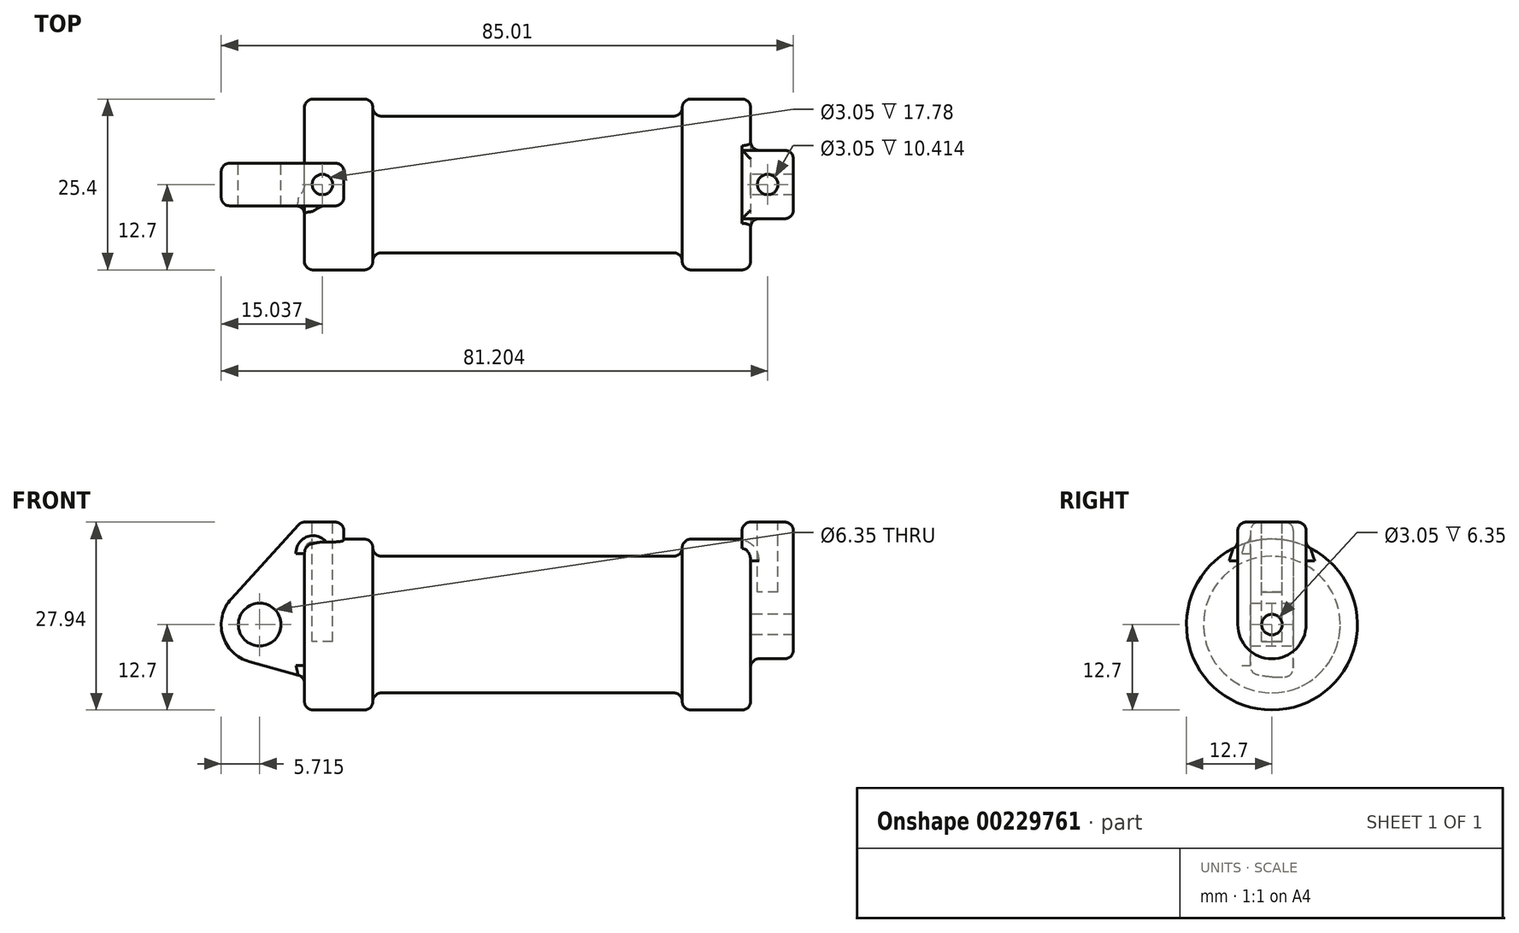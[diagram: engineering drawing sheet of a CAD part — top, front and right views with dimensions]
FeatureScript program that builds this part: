
annotation { "Feature Type Name" : "Feature", "Feature Type Description" : "" }
export const myFeature = defineFeature(function(context is Context, id is Id, definition is map)
    precondition{}
    {
        {
            var Q0;
            Q0=qCreatedBy(makeId("Front.planeOp"),FACE);
            var sketch = newSketch(context, id + "F0", { "sketchPlane" : qUnion([Q0])});
            skLineSegment(sketch, "E0", {"start": v(0, 0) * mm, "end": v(0, 12.7) * mm});
            skLineSegment(sketch, "E1", {"start": v(0, 12.7) * mm, "end": v(10.16, 12.7) * mm});
            skLineSegment(sketch, "E2", {"start": v(10.16, 12.7) * mm, "end": v(10.16, 10.16) * mm});
            skLineSegment(sketch, "E3", {"start": v(10.16, 10.16) * mm, "end": v(56.13, 10.16) * mm});
            skLineSegment(sketch, "E4", {"start": v(56.13, 10.16) * mm, "end": v(56.13, 12.7) * mm});
            skLineSegment(sketch, "E5", {"start": v(56.13, 12.7) * mm, "end": v(66.3, 12.7) * mm});
            skLineSegment(sketch, "E6", {"start": v(66.3, 12.7) * mm, "end": v(66.3, 0) * mm});
            skLineSegment(sketch, "E7", {"start": v(66.3, 0) * mm, "end": v(0, 0) * mm});
            skLineSegment(sketch, "E8", {"start": v(5.84, 15.24) * mm, "end": v(-0.5, 15.24) * mm});
            skLineSegment(sketch, "E9", {"start": v(-0.5, 15.24) * mm, "end": v(-10.88, 3.85) * mm});
            skLineSegment(sketch, "E10", {"start": v(0, 0) * mm, "end": v(-6.65, 0) * mm});
            skCircle(sketch, "E11", {"center": v(-6.65, 0) * mm, "radius": 5.72 * mm});
            skCircle(sketch, "E12", {"center": v(-6.65, 0) * mm, "radius": 3.18 * mm});
            skLineSegment(sketch, "E13", {"start": v(5.84, 15.24) * mm, "end": v(5.84, -9.4) * mm});
            skLineSegment(sketch, "E14", {"start": v(5.84, -9.4) * mm, "end": v(-8.18, -5.5) * mm});
            skSolve(sketch);
        }
        {
            var Q0;
            {var subQ0=sQuery(id+"F0.wireOp",EDGE,"E0");Q0=makeQuery(id+"F0.imprint","IMPRINT",FACE,{"disambiguationData":[TD([[makeQuery(id+"F0.imprint","IMPRINT",EDGE,{"derivedFrom":subQ0}),-1.0]])]});}
            var Q1;
            {var subQ0=sQuery(id+"F0.wireOp",EDGE,"E2");Q1=makeQuery(id+"F0.imprint","IMPRINT",FACE,{"disambiguationData":[TD([[makeQuery(id+"F0.imprint","IMPRINT",EDGE,{"derivedFrom":subQ0}),-1.0]])]});}
            var Q2;
            Q2=sQuery(id+"F0.wireOp",EDGE,"E7");
            revolve(context, id + "F1", {"entities" : qUnion([Q0, Q1]), "axis" : qUnion([Q2]), "revolveType" : RevolveType.FULL});
        }
        {
            var Q0;
            {var subQ3=sQuery(id+"F0.wireOp",EDGE,"E0");Q0=makeQuery(id+"F0.imprint","IMPRINT",FACE,{"disambiguationData":[TD([[makeQuery(id+"F0.imprint","IMPRINT",EDGE,{"derivedFrom":subQ3}),1.0]])]});}
            var Q1;
            {var subQ0=sQuery(id+"F0.wireOp",EDGE,"E0");Q1=makeQuery(id+"F0.imprint","IMPRINT",FACE,{"disambiguationData":[TD([[makeQuery(id+"F0.imprint","IMPRINT",EDGE,{"derivedFrom":subQ0}),-1.0]])]});}
            var Q2;
            {var subQ4=sQuery(id+"F0.wireOp",EDGE,"E12");Q2=makeQuery(id+"F0.imprint","IMPRINT",FACE,{"disambiguationData":[TD([[makeQuery(id+"F0.imprint","IMPRINT",EDGE,{"derivedFrom":subQ4}),-1.0]])]});}
            var Q3;
            {var subQ0=sQuery(id+"F0.wireOp",EDGE,"E14");Q3=makeQuery(id+"F0.imprint","IMPRINT",FACE,{"disambiguationData":[TD([[makeQuery(id+"F0.imprint","IMPRINT",EDGE,{"derivedFrom":subQ0}),-1.0]])]});}
            extrude(context, id + "F2", {"entities" : qUnion([Q0, Q1, Q2, Q3]), "operationType" : NewBodyOperationType.ADD, "endBound" : BoundingType.SYMMETRIC, "depth" : 6.35 * mm});
        }
        {
            var Q0;
            Q0=makeQuery(id+"F1.opRevolve","SWEPT_FACE",FACE,{"disambiguationData":[OSD([sQuery(id+"F0.wireOp",EDGE,"E6")])]});
            var sketch = newSketch(context, id + "F3", { "sketchPlane" : qUnion([Q0])});
            skCircle(sketch, "E15", {"center": v(0, 0) * mm, "radius": 1.52 * mm});
            skCircle(sketch, "E16", {"center": v(0, 0) * mm, "radius": 5.08 * mm});
            skLineSegment(sketch, "E17", {"start": v(5.08, 0) * mm, "end": v(5.08, 15.24) * mm});
            skLineSegment(sketch, "E18", {"start": v(5.08, 15.24) * mm, "end": v(-5.08, 15.24) * mm});
            skLineSegment(sketch, "E19", {"start": v(-5.08, 15.24) * mm, "end": v(-5.08, 0) * mm});
            skSolve(sketch);
        }
        {
            var Q0;
            Q0=qSketchRegion(id+"F3",true);
            var Q1;
            Q1=qSketchRegion(id+"F5",true);
            extrude(context, id + "F4", {"entities" : qUnion([Q0, Q1]), "operationType" : NewBodyOperationType.ADD, "depth" : 6.35 * mm, "hasSecondDirection" : true, "secondDirectionOppositeDirection" : true, "secondDirectionDepth" : 1.27 * mm});
        }
        {
            var Q0;
            Q0=makeQuery(id+"F2.opExtrude","SWEPT_FACE",FACE,{"disambiguationData":[OSD([sQuery(id+"F0.wireOp",EDGE,"E8")])]});
            var sketch = newSketch(context, id + "F5", { "sketchPlane" : qUnion([Q0])});
            skCircle(sketch, "E20", {"center": v(2.67, 0) * mm, "radius": 1.52 * mm});
            skPoint(sketch, "E20.centerSnap0", {"position": v(5.84, 0) * mm});
            skPoint(sketch, "E20.centerSnap1", {"position": v(2.67, 3.18) * mm});
            skCircle(sketch, "E21", {"center": v(68.83, 0) * mm, "radius": 1.52 * mm});
            skPoint(sketch, "E21.centerSnap0", {"position": v(72.64, 0) * mm});
            skPoint(sketch, "E21.centerSnap1", {"position": v(68.83, 5.08) * mm});
            skSolve(sketch);
        }
        {
            var Q0;
            Q0=makeQuery(id+"F5.imprint","IMPRINT",FACE,{"disambiguationData":[TD([[makeQuery(id+"F5.imprint","IMPRINT",EDGE,{"derivedFrom":sQuery(id+"F5.wireOp",EDGE,"E20")}),1.0]])]});
            var Q1;
            Q1=sQuery(id+"F5.wireOp",EDGE,"E21");
            extrude(context, id + "F6", {"entities" : qUnion([Q0]), "operationType" : NewBodyOperationType.REMOVE, "surfaceEntities" : qUnion([Q1]), "oppositeDirection" : true, "depth" : 17.78 * mm});
        }
        {
            var Q0;
            Q0=makeQuery(id+"F5.imprint","IMPRINT",FACE,{"disambiguationData":[TD([[makeQuery(id+"F5.imprint","IMPRINT",EDGE,{"derivedFrom":sQuery(id+"F5.wireOp",EDGE,"E21")}),1.0]])]});
            extrude(context, id + "F7", {"entities" : qUnion([Q0]), "operationType" : NewBodyOperationType.REMOVE, "oppositeDirection" : true, "depth" : 10.4 * mm});
        }
        {
            var Q0;
            Q0=makeQuery(id+"F1.opRevolve","SWEPT_FACE",FACE,{"disambiguationData":[OSD([sQuery(id+"F0.wireOp",EDGE,"E3")])]});
            var Q1;
            Q1=makeQuery(id+"F1.opRevolve","SWEPT_EDGE",EDGE,{"disambiguationData":[OSD([sQuery(id+"F0.wireOp",EDGE,"E4"),sQuery(id+"F0.wireOp",EDGE,"E5")])]});
            var Q2;
            Q2=makeQuery(id+"F1.opRevolve","SWEPT_EDGE",EDGE,{"disambiguationData":[OSD([sQuery(id+"F0.wireOp",EDGE,"E1"),sQuery(id+"F0.wireOp",EDGE,"E2")])]});
            var Q3;
            Q3=makeQuery(id+"F1.opRevolve","SWEPT_EDGE",EDGE,{"disambiguationData":[OSD([sQuery(id+"F0.wireOp",EDGE,"E0"),sQuery(id+"F0.wireOp",EDGE,"E1")])]});
            var Q4;
            Q4=makeQuery(id+"F2.boolean.opBoolean","INTERSECT",EDGE,{"derivedFrom":[makeQuery(id+"F1.opRevolve","SWEPT_FACE",FACE,{"disambiguationData":[OSD([sQuery(id+"F0.wireOp",EDGE,"E0")])]}),makeQuery(id+"F2.opExtrude","CAP_FACE",FACE,{"disambiguationData":[OSD([sQuery(id+"F0.wireOp",EDGE,"E8"),sQuery(id+"F0.wireOp",EDGE,"E9"),sQuery(id+"F0.wireOp",EDGE,"E11"),sQuery(id+"F0.wireOp",EDGE,"E12"),sQuery(id+"F0.wireOp",EDGE,"E13"),sQuery(id+"F0.wireOp",EDGE,"E14")])],"isStart":false})]});
            var Q5;
            Q5=makeQuery(id+"F2.opExtrude","CAP_EDGE",EDGE,{"disambiguationData":[OSD([sQuery(id+"F0.wireOp",EDGE,"E9")])],"isStart":false});
            var Q6;
            Q6=makeQuery(id+"F2.opExtrude","CAP_EDGE",EDGE,{"disambiguationData":[OSD([sQuery(id+"F0.wireOp",EDGE,"E8")])],"isStart":false});
            var Q7;
            Q7=makeQuery(id+"F2.opExtrude","CAP_EDGE",EDGE,{"disambiguationData":[OSD([sQuery(id+"F0.wireOp",EDGE,"E8")])],"isStart":true});
            var Q8;
            Q8=makeQuery(id+"F2.opExtrude","SWEPT_EDGE",EDGE,{"disambiguationData":[OSD([sQuery(id+"F0.wireOp",EDGE,"E8"),sQuery(id+"F0.wireOp",EDGE,"E13")])]});
            var Q9;
            Q9=makeQuery(id+"F2.opExtrude","CAP_EDGE",EDGE,{"disambiguationData":[OSD([sQuery(id+"F0.wireOp",EDGE,"E13")])],"isStart":false});
            var Q10;
            Q10=makeQuery(id+"F2.opExtrude","CAP_EDGE",EDGE,{"disambiguationData":[OSD([sQuery(id+"F0.wireOp",EDGE,"E9")])],"isStart":true});
            var Q11;
            Q11=makeQuery(id+"F2.opExtrude","CAP_EDGE",EDGE,{"disambiguationData":[OSD([sQuery(id+"F0.wireOp",EDGE,"E13")])],"isStart":true});
            var Q12;
            Q12=makeQuery(id+"F4.opExtrude","CAP_EDGE",EDGE,{"disambiguationData":[OSD([sQuery(id+"F3.wireOp",EDGE,"E19")])],"isStart":false});
            var Q13;
            Q13=makeQuery(id+"F1.opRevolve","SWEPT_EDGE",EDGE,{"disambiguationData":[OSD([sQuery(id+"F0.wireOp",EDGE,"E5"),sQuery(id+"F0.wireOp",EDGE,"E6")])]});
            var Q14;
            Q14=makeQuery(id+"F4.opExtrude","SWEPT_EDGE",EDGE,{"disambiguationData":[OSD([sQuery(id+"F3.wireOp",EDGE,"E18"),sQuery(id+"F3.wireOp",EDGE,"E19")])]});
            var Q15;
            Q15=makeQuery(id+"F4.opExtrude","CAP_EDGE",EDGE,{"disambiguationData":[OSD([sQuery(id+"F3.wireOp",EDGE,"E18")])],"isStart":false});
            var Q16;
            Q16=makeQuery(id+"F4.opExtrude","SWEPT_EDGE",EDGE,{"disambiguationData":[OSD([sQuery(id+"F3.wireOp",EDGE,"E17"),sQuery(id+"F3.wireOp",EDGE,"E18")])]});
            var Q17;
            Q17=makeQuery(id+"F4.opExtrude","CAP_EDGE",EDGE,{"disambiguationData":[OSD([sQuery(id+"F3.wireOp",EDGE,"E18")])],"isStart":true});
            var Q18;
            Q18=makeQuery(id+"F4.boolean.opBoolean","INTERSECT",EDGE,{"derivedFrom":[makeQuery(id+"F1.opRevolve","SWEPT_FACE",FACE,{"disambiguationData":[OSD([sQuery(id+"F0.wireOp",EDGE,"E6")])]}),makeQuery(id+"F4.opExtrude","SWEPT_FACE",FACE,{"disambiguationData":[OSD([sQuery(id+"F3.wireOp",EDGE,"E19")])]})]});
            var Q19;
            Q19=makeQuery(id+"F2.opExtrude","SWEPT_EDGE",EDGE,{"disambiguationData":[OSD([sQuery(id+"F0.wireOp",EDGE,"E8"),sQuery(id+"F0.wireOp",EDGE,"E9")])]});
            fillet(context, id + "F8", {"entities" : qUnion([Q0, Q1, Q2, Q3, Q4, Q5, Q6, Q7, Q8, Q9, Q10, Q11, Q12, Q13, Q14, Q15, Q16, Q17, Q18, Q19]), "radius" : 1.27 * mm, "tangentPropagation" : true, "allowEdgeOverflow" : false});
        }
    });
